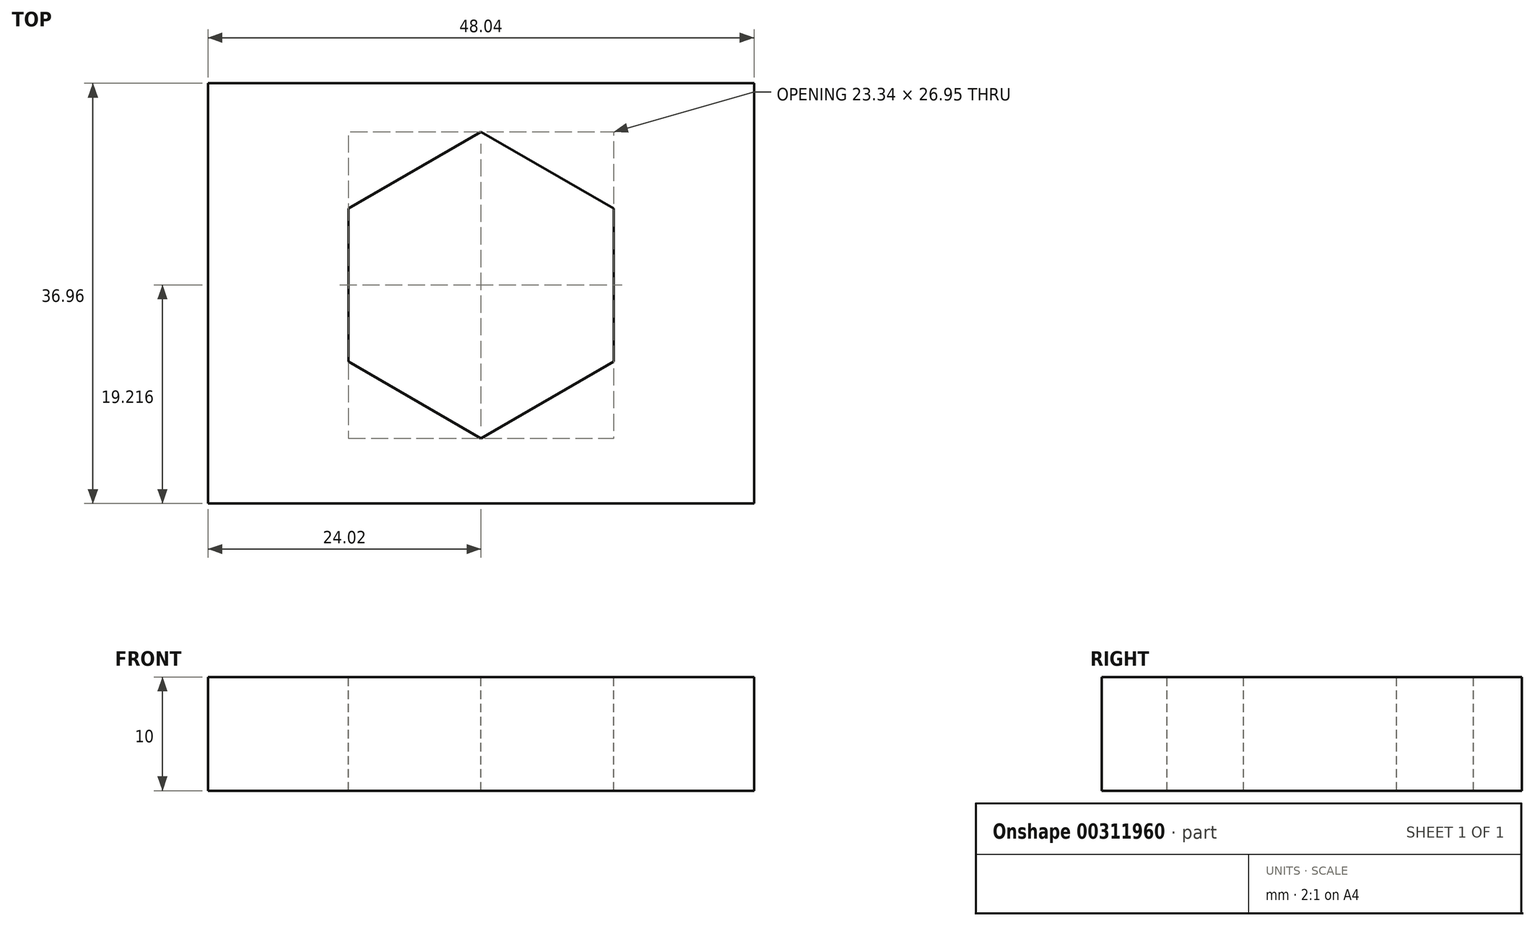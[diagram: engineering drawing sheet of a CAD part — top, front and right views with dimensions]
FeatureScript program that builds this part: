
annotation { "Feature Type Name" : "Feature", "Feature Type Description" : "" }
export const myFeature = defineFeature(function(context is Context, id is Id, definition is map)
    precondition{}
    {
        {
            var Q0;
            Q0=qCreatedBy(makeId("Top.planeOp"),FACE);
            var sketch = newSketch(context, id + "F0", { "sketchPlane" : qUnion([Q0])});
            skLineSegment(sketch, "E0.bottom", {"start": v(0, 0) * mm, "end": v(-48.04, 0) * mm});
            skLineSegment(sketch, "E0.top", {"start": v(0, -36.96) * mm, "end": v(-48.04, -36.96) * mm});
            skLineSegment(sketch, "E0.left", {"start": v(0, 0) * mm, "end": v(0, -36.96) * mm});
            skLineSegment(sketch, "E0.right", {"start": v(-48.04, 0) * mm, "end": v(-48.04, -36.96) * mm});
            skLineSegment(sketch, "E1.bottom", {"start": v(0, -18.48) * mm, "end": v(0, -18.48) * mm});
            skLineSegment(sketch, "E1.top", {"start": v(0, -18.48) * mm, "end": v(0, -18.48) * mm});
            skLineSegment(sketch, "E1.left", {"start": v(0, -18.48) * mm, "end": v(0, -18.48) * mm});
            skLineSegment(sketch, "E1.right", {"start": v(0, -18.48) * mm, "end": v(0, -18.48) * mm});
            skSolve(sketch);
        }
        {
            var Q0;
            Q0=makeQuery(id+"F0.imprint","IMPRINT",FACE,{"disambiguationData":[TD([[makeQuery(id+"F0.imprint","IMPRINT",EDGE,{"derivedFrom":sQuery(id+"F0.wireOp",EDGE,"E0.bottom")}),1.0]])]});
            extrude(context, id + "F1", {"entities" : qUnion([Q0]), "depth" : 10 * mm});
        }
        {
            var Q0;
            Q0=makeQuery(id+"F1.opExtrude","CAP_FACE",FACE,{"disambiguationData":[OSD([sQuery(id+"F0.wireOp",EDGE,"E0.bottom"),sQuery(id+"F0.wireOp",EDGE,"E0.top"),sQuery(id+"F0.wireOp",EDGE,"E0.left"),sQuery(id+"F0.wireOp",EDGE,"E0.right")])],"isStart":false});
            var sketch = newSketch(context, id + "F2", { "sketchPlane" : qUnion([Q0])});
            skCircle(sketch, "E2.cCircle", {"center": v(-24.02, -17.74) * mm, "radius": 11.67 * mm, "construction": true});
            skPoint(sketch, "E2.cCircle.centerSnap0", {"position": v(-24.02, 0) * mm});
            skLineSegment(sketch, "E2.0", {"start": v(-12.35, -11) * mm, "end": v(-12.35, -24.48) * mm});
            skLineSegment(sketch, "E2.1", {"start": v(-12.35, -24.48) * mm, "end": v(-24.02, -31.22) * mm});
            skLineSegment(sketch, "E2.2", {"start": v(-24.02, -31.22) * mm, "end": v(-35.7, -24.48) * mm});
            skLineSegment(sketch, "E2.3", {"start": v(-35.7, -24.48) * mm, "end": v(-35.7, -11) * mm});
            skLineSegment(sketch, "E2.4", {"start": v(-35.7, -11) * mm, "end": v(-24.02, -4.27) * mm});
            skLineSegment(sketch, "E2.5", {"start": v(-24.02, -4.27) * mm, "end": v(-12.35, -11) * mm});
            skPoint(sketch, "E2.0.midPoint", {"position": v(-12.35, -17.74) * mm});
            skSolve(sketch);
        }
        {
            var Q0;
            Q0=makeQuery(id+"F2.imprint","IMPRINT",FACE,{"disambiguationData":[TD([[makeQuery(id+"F2.imprint","IMPRINT",EDGE,{"derivedFrom":sQuery(id+"F2.wireOp",EDGE,"E2.0")}),-1.0]])]});
            extrude(context, id + "F3", {"entities" : qUnion([Q0]), "operationType" : NewBodyOperationType.REMOVE, "oppositeDirection" : true, "depth" : 25.4 * mm});
        }
    });
